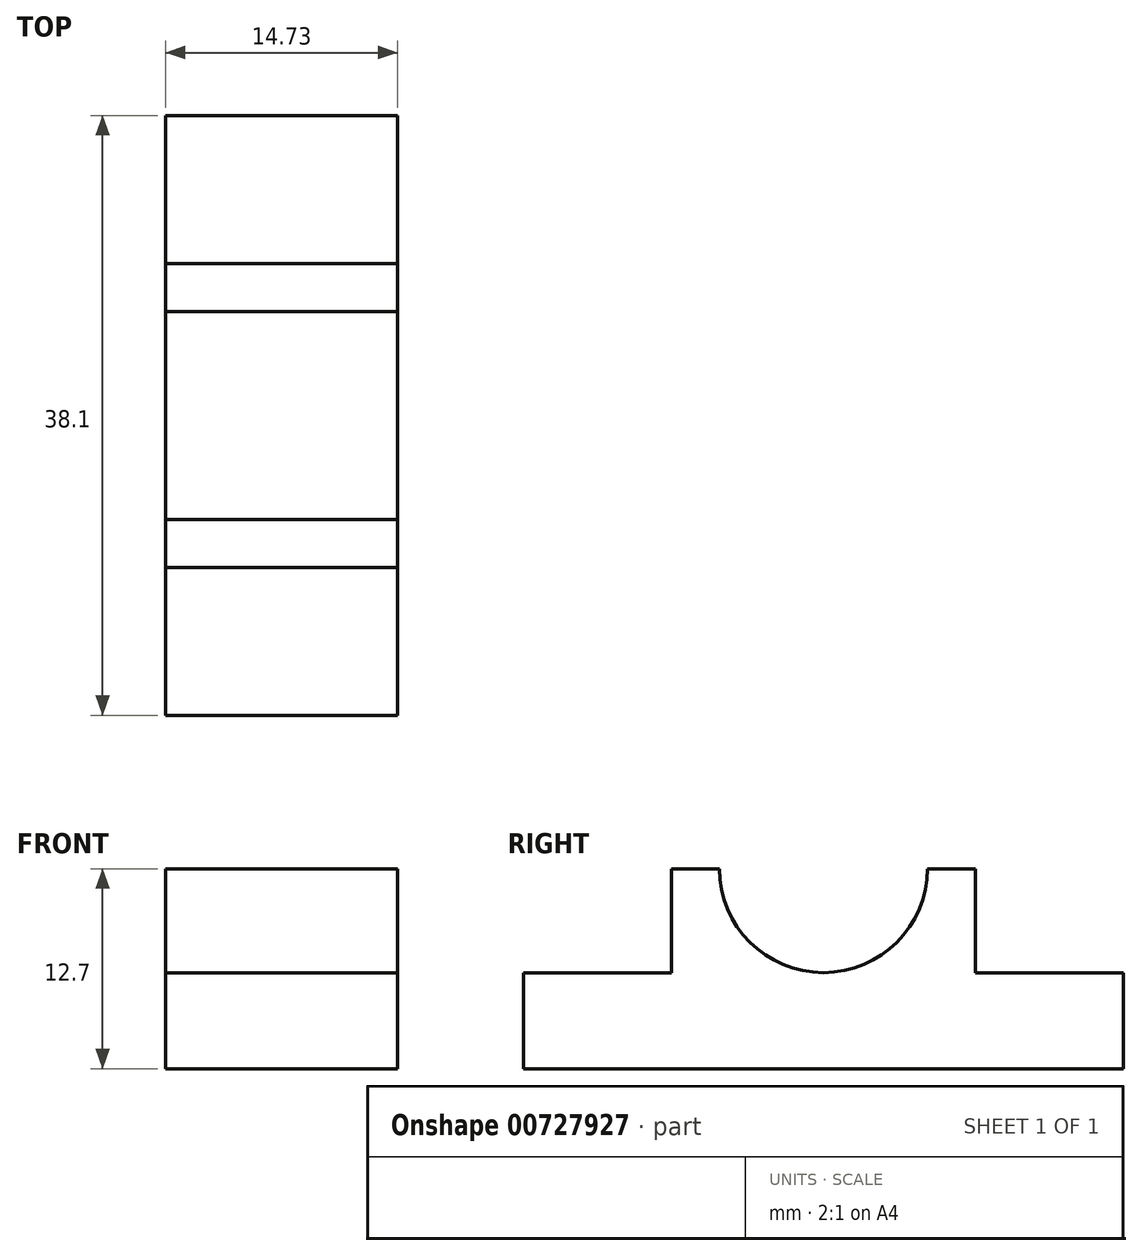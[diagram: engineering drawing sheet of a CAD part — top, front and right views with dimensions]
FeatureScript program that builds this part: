
annotation { "Feature Type Name" : "Feature", "Feature Type Description" : "" }
export const myFeature = defineFeature(function(context is Context, id is Id, definition is map)
    precondition{}
    {
        {
            var Q0;
            Q0=qCreatedBy(makeId("Right.planeOp"),FACE);
            var sketch = newSketch(context, id + "F0", { "sketchPlane" : qUnion([Q0])});
            skLineSegment(sketch, "E0", {"start": v(-60.82, -20.82) * mm, "end": v(-22.72, -20.82) * mm});
            skLineSegment(sketch, "E1", {"start": v(-60.82, -20.82) * mm, "end": v(-60.82, -14.72) * mm});
            skLineSegment(sketch, "E2", {"start": v(-60.82, -14.72) * mm, "end": v(-51.42, -14.72) * mm});
            skLineSegment(sketch, "E3", {"start": v(-51.42, -14.72) * mm, "end": v(-51.42, -8.12) * mm});
            skLineSegment(sketch, "E4", {"start": v(-51.42, -8.12) * mm, "end": v(-32.12, -8.12) * mm});
            skLineSegment(sketch, "E5", {"start": v(-32.12, -8.12) * mm, "end": v(-32.12, -14.72) * mm});
            skLineSegment(sketch, "E6", {"start": v(-32.12, -14.72) * mm, "end": v(-22.72, -14.72) * mm});
            skLineSegment(sketch, "E7", {"start": v(-22.72, -14.72) * mm, "end": v(-22.72, -20.82) * mm});
            skSolve(sketch);
        }
        {
            var Q0;
            Q0=makeQuery(id+"F0.imprint","IMPRINT",FACE,{"disambiguationData":[TD([[makeQuery(id+"F0.imprint","IMPRINT",EDGE,{"derivedFrom":sQuery(id+"F0.wireOp",EDGE,"E0")}),1.0]])]});
            extrude(context, id + "F1", {"entities" : qUnion([Q0]), "depth" : 14.73 * mm, "offsetDistance" : 25.4 * mm});
        }
        {
            var Q0;
            Q0=makeQuery(id+"F1.opExtrude","CAP_FACE",FACE,{"disambiguationData":[OSD([sQuery(id+"F0.wireOp",EDGE,"E0"),sQuery(id+"F0.wireOp",EDGE,"E1"),sQuery(id+"F0.wireOp",EDGE,"E2"),sQuery(id+"F0.wireOp",EDGE,"E3"),sQuery(id+"F0.wireOp",EDGE,"E4"),sQuery(id+"F0.wireOp",EDGE,"E5"),sQuery(id+"F0.wireOp",EDGE,"E6"),sQuery(id+"F0.wireOp",EDGE,"E7")])],"isStart":false});
            var sketch = newSketch(context, id + "F2", { "sketchPlane" : qUnion([Q0])});
            skCircle(sketch, "E8", {"center": v(-41.77, -8.12) * mm, "radius": 6.6 * mm});
            skSolve(sketch);
        }
        {
            var Q0;
            {var subQ0=sQuery(id+"F2.wireOp",EDGE,"E8");var subQ1=makeQuery(id+"F1.opExtrude","CAP_EDGE",EDGE,{"disambiguationData":[OSD([sQuery(id+"F0.wireOp",EDGE,"E4")])],"isStart":false});var subQ2=makeQuery(id+"F2.imprint","INTERSECT",VERTEX,{"disambiguationData":[OD(0.0)],"derivedFrom":[subQ1,subQ0]});Q0=makeQuery(id+"F2.imprint","IMPRINT",FACE,{"disambiguationData":[TD([[makeQuery(id+"F2.imprint","IMPRINT",EDGE,{"disambiguationData":[TD([[subQ2,-1.0]])],"derivedFrom":subQ0}),1.0]])]});}
            extrude(context, id + "F3", {"entities" : qUnion([Q0]), "operationType" : NewBodyOperationType.REMOVE, "oppositeDirection" : true, "depth" : 14.73 * mm, "offsetDistance" : 25.4 * mm});
        }
    });
